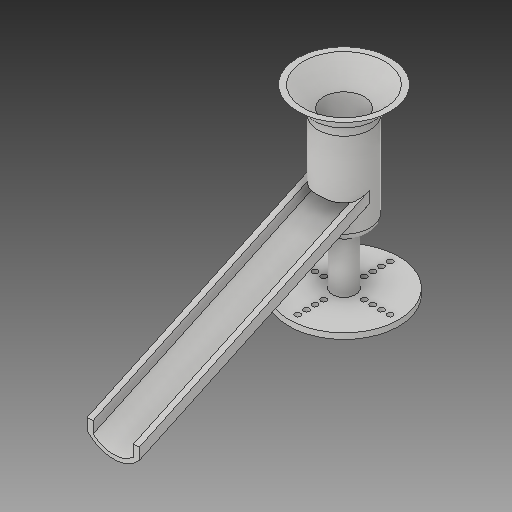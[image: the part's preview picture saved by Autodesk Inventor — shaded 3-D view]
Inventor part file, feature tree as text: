
AUTODESK INVENTOR PART (.ipt)
format: ipt  version: 2019 (Build 230136000, 136)  size: 320,512 bytes
history: native  units: mm
features: sketch x10, extrude x7, sweep x4, other x2, fillet x2, mirror x1, pattern_circular x1
ambient origin geometry x8: Origin, YZ Plane, XZ Plane, XY Plane, X Axis, Y Axis, Z Axis, Center Point
bodies: Solide1 (feature_tree)
feature tree (27):
  sketch  "Esquisse2"
  sketch  "Esquisse1"
  sweep  "Balayage1"
  sweep  "Balayage2"
  extrude  "Extrusion1"  Depth=20.071286mm
  other  "Plan de construction1"
  sketch  "Esquisse4"
  extrude  "Extrusion2"  Depth=7.0mm
  sweep  "Balayage3"
  extrude  "Extrusion3"  Depth=2.0mm
  extrude  "Extrusion4"  Depth=4.0mm
  sweep  "Balayage4"
  extrude  "Extrusion5"  TaperAngle=0.0deg  [1 undecoded]
  extrude  "Extrusion6"  Depth=15.0mm TaperAngle=0.0deg
  fillet  "Congé1"  Radius=10.0mm
  extrude  "Extrusion7"  Depth=11.34464mm
  mirror  "Symétrie1"
  pattern_circular  "Réseau circulaire1"  [2 undecoded]
  other  "Révolution1"
  fillet  "Congé2"  Radius=20.0mm
  sketch  "Esquisse3"
  sketch  "Esquisse6"
  sketch  "Esquisse7"
  sketch  "Esquisse9"
  sketch  "Esquisse10"
  sketch  "Esquisse11"
  sketch  "Esquisse12"
note: 3 required parameter values undecoded (feature->parameter linkage not recoverable at this tier; creation-order binding heuristic only, values carry confidence <= 0.55)
